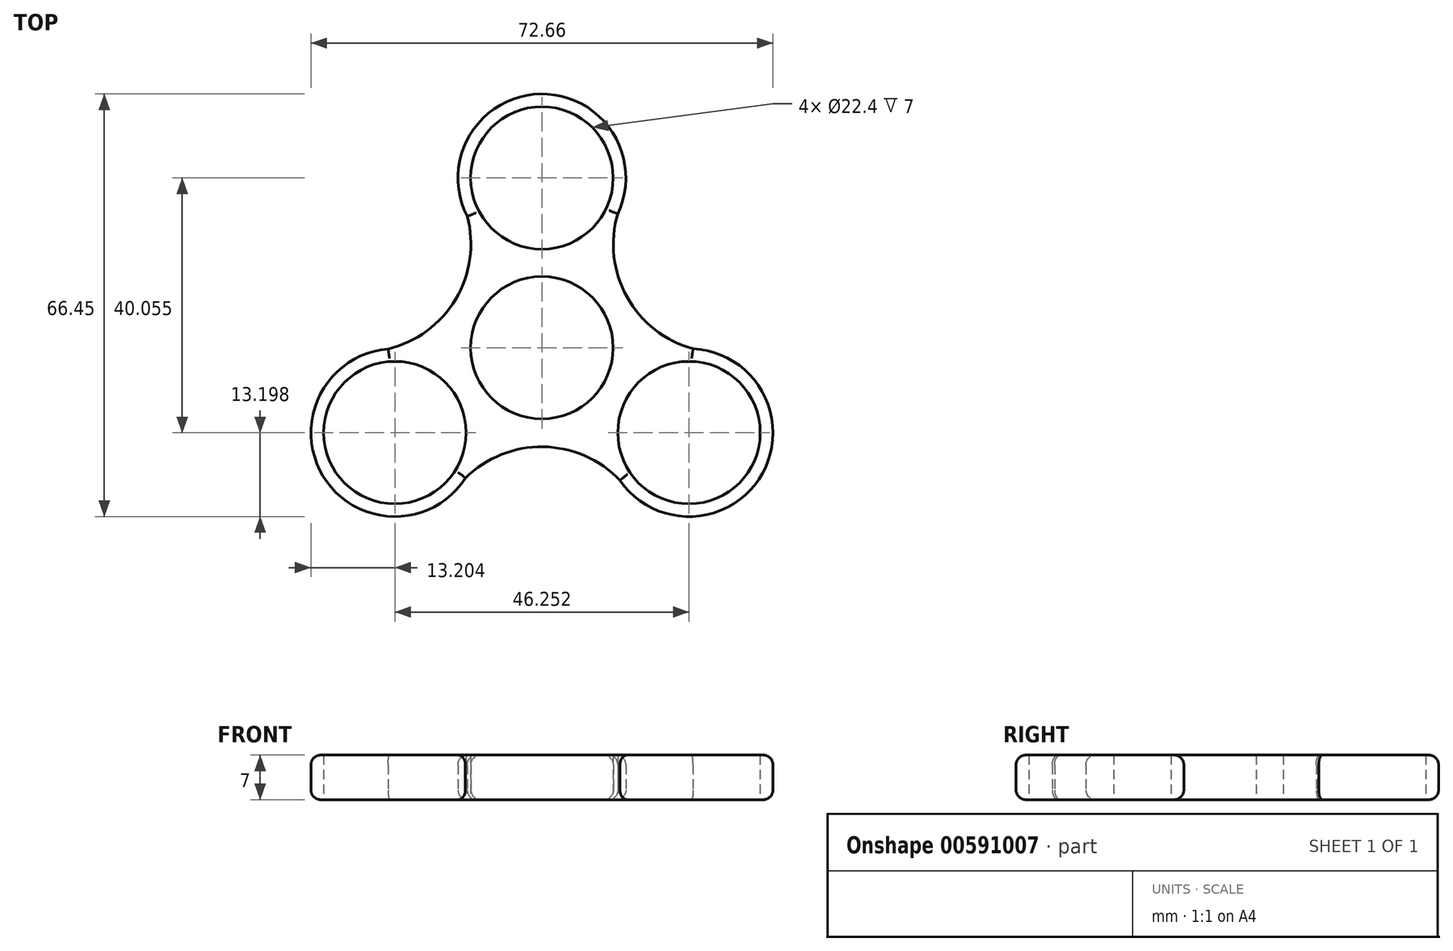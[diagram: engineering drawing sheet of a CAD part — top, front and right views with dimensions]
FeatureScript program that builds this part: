
annotation { "Feature Type Name" : "Feature", "Feature Type Description" : "" }
export const myFeature = defineFeature(function(context is Context, id is Id, definition is map)
    precondition{}
    {
        {
            var Q0;
            Q0=qCreatedBy(makeId("Top.planeOp"),FACE);
            var sketch = newSketch(context, id + "F0", { "sketchPlane" : qUnion([Q0])});
            skCircle(sketch, "E0", {"center": v(0, 0) * mm, "radius": 11.2 * mm});
            skCircle(sketch, "E1", {"center": v(0, 26.7) * mm, "radius": 11.2 * mm});
            skArc(sketch, "E2", {"start": v(11.93, 21.05) * mm, "mid": v(-0.22, 39.9) * mm, "end": v(-11.74, 20.67) * mm});
            skCircle(sketch, "E3.1.0", {"center": v(-23.13, -13.35) * mm, "radius": 11.2 * mm});
            skArc(sketch, "E3.1.1", {"start": v(-24.2, -0.2) * mm, "mid": v(-34.45, -20.14) * mm, "end": v(-12.03, -20.5) * mm});
            skCircle(sketch, "E3.2.0", {"center": v(23.13, -13.35) * mm, "radius": 11.2 * mm});
            skArc(sketch, "E3.2.1", {"start": v(12.27, -20.86) * mm, "mid": v(34.66, -19.76) * mm, "end": v(23.77, -0.17) * mm});
            skArc(sketch, "E4", {"start": v(11.93, 21.05) * mm, "mid": v(13.39, 7.96) * mm, "end": v(23.77, -0.17) * mm});
            skArc(sketch, "E5.1.0", {"start": v(-24.2, -0.2) * mm, "mid": v(-13.58, 7.62) * mm, "end": v(-11.74, 20.67) * mm});
            skArc(sketch, "E5.2.0", {"start": v(12.27, -20.86) * mm, "mid": v(0.2, -15.57) * mm, "end": v(-12.03, -20.5) * mm});
            skLineSegment(sketch, "E6.trimOffspring", {"start": v(16.53, -1.92) * mm, "end": v(17.53, -3.65) * mm, "construction": true});
            skSolve(sketch);
        }
        {
            var Q0;
            Q0=makeQuery(id+"F0.imprint","IMPRINT",FACE,{"disambiguationData":[TD([[makeQuery(id+"F0.imprint","IMPRINT",EDGE,{"derivedFrom":sQuery(id+"F0.wireOp",EDGE,"E0")}),-1.0]])]});
            extrude(context, id + "F1", {"entities" : qUnion([Q0]), "depth" : 7 * mm, "offsetDistance" : 25 * mm});
        }
        {
            var Q0;
            Q0=makeQuery(id+"F1.opExtrude","CAP_EDGE",EDGE,{"disambiguationData":[OSD([sQuery(id+"F0.wireOp",EDGE,"E5.2.0")])],"isStart":false});
            var Q1;
            Q1=makeQuery(id+"F1.opExtrude","CAP_EDGE",EDGE,{"disambiguationData":[OSD([sQuery(id+"F0.wireOp",EDGE,"E5.2.0")])],"isStart":true});
            var Q2;
            Q2=makeQuery(id+"F1.opExtrude","CAP_EDGE",EDGE,{"disambiguationData":[OSD([sQuery(id+"F0.wireOp",EDGE,"E3.1.1")])],"isStart":false});
            var Q3;
            Q3=makeQuery(id+"F1.opExtrude","CAP_EDGE",EDGE,{"disambiguationData":[OSD([sQuery(id+"F0.wireOp",EDGE,"E5.1.0")])],"isStart":false});
            var Q4;
            Q4=makeQuery(id+"F1.opExtrude","CAP_EDGE",EDGE,{"disambiguationData":[OSD([sQuery(id+"F0.wireOp",EDGE,"E4")])],"isStart":false});
            var Q5;
            Q5=makeQuery(id+"F1.opExtrude","CAP_EDGE",EDGE,{"disambiguationData":[OSD([sQuery(id+"F0.wireOp",EDGE,"E2")])],"isStart":false});
            var Q6;
            Q6=makeQuery(id+"F1.opExtrude","CAP_EDGE",EDGE,{"disambiguationData":[OSD([sQuery(id+"F0.wireOp",EDGE,"E3.2.1")])],"isStart":false});
            fillet(context, id + "F2", {"entities" : qUnion([Q0, Q1, Q2, Q3, Q4, Q5, Q6]), "radius" : 1.5 * mm, "tangentPropagation" : true, "allowEdgeOverflow" : false});
        }
        {
            var Q0;
            Q0=makeQuery(id+"F1.opExtrude","CAP_EDGE",EDGE,{"disambiguationData":[OSD([sQuery(id+"F0.wireOp",EDGE,"E3.1.1")])],"isStart":true});
            var Q1;
            Q1=makeQuery(id+"F1.opExtrude","CAP_EDGE",EDGE,{"disambiguationData":[OSD([sQuery(id+"F0.wireOp",EDGE,"E5.1.0")])],"isStart":true});
            var Q2;
            Q2=makeQuery(id+"F1.opExtrude","CAP_EDGE",EDGE,{"disambiguationData":[OSD([sQuery(id+"F0.wireOp",EDGE,"E2")])],"isStart":true});
            var Q3;
            Q3=makeQuery(id+"F1.opExtrude","CAP_EDGE",EDGE,{"disambiguationData":[OSD([sQuery(id+"F0.wireOp",EDGE,"E4")])],"isStart":true});
            var Q4;
            Q4=makeQuery(id+"F1.opExtrude","CAP_EDGE",EDGE,{"disambiguationData":[OSD([sQuery(id+"F0.wireOp",EDGE,"E3.2.1")])],"isStart":true});
            fillet(context, id + "F3", {"entities" : qUnion([Q0, Q1, Q2, Q3, Q4]), "radius" : 1.5 * mm, "tangentPropagation" : true, "allowEdgeOverflow" : false});
        }
    });
